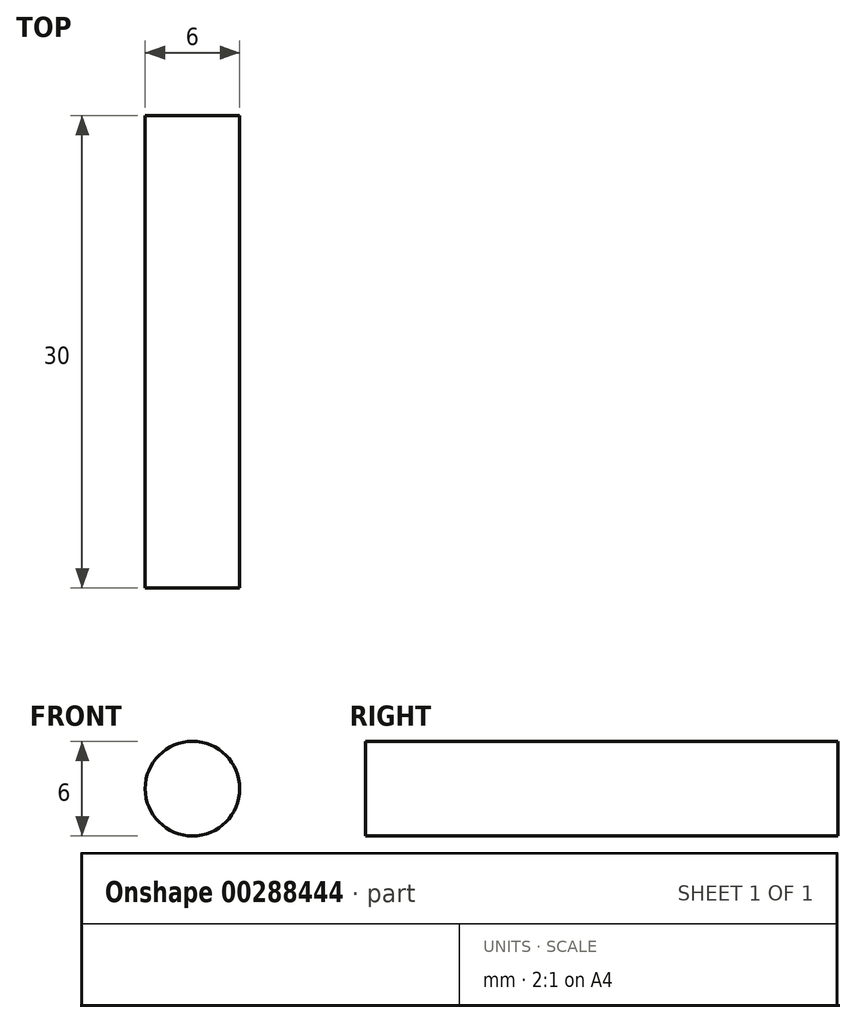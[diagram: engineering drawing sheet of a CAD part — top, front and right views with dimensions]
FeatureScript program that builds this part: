
annotation { "Feature Type Name" : "Feature", "Feature Type Description" : "" }
export const myFeature = defineFeature(function(context is Context, id is Id, definition is map)
    precondition{}
    {
        {
            var Q0;
            Q0=qCreatedBy(makeId("Front.planeOp"),FACE);
            var sketch = newSketch(context, id + "F0", { "sketchPlane" : qUnion([Q0])});
            skCircle(sketch, "E0", {"center": v(0, 0) * mm, "radius": 3 * mm});
            skSolve(sketch);
        }
        {
            var Q0;
            Q0 = qSketchRegion(id + "F0", true);
            extrude(context, id + "F1", {"entities" : qUnion([Q0]), "endBound" : BoundingType.SYMMETRIC, "depth" : 30 * mm});
        }
    });
